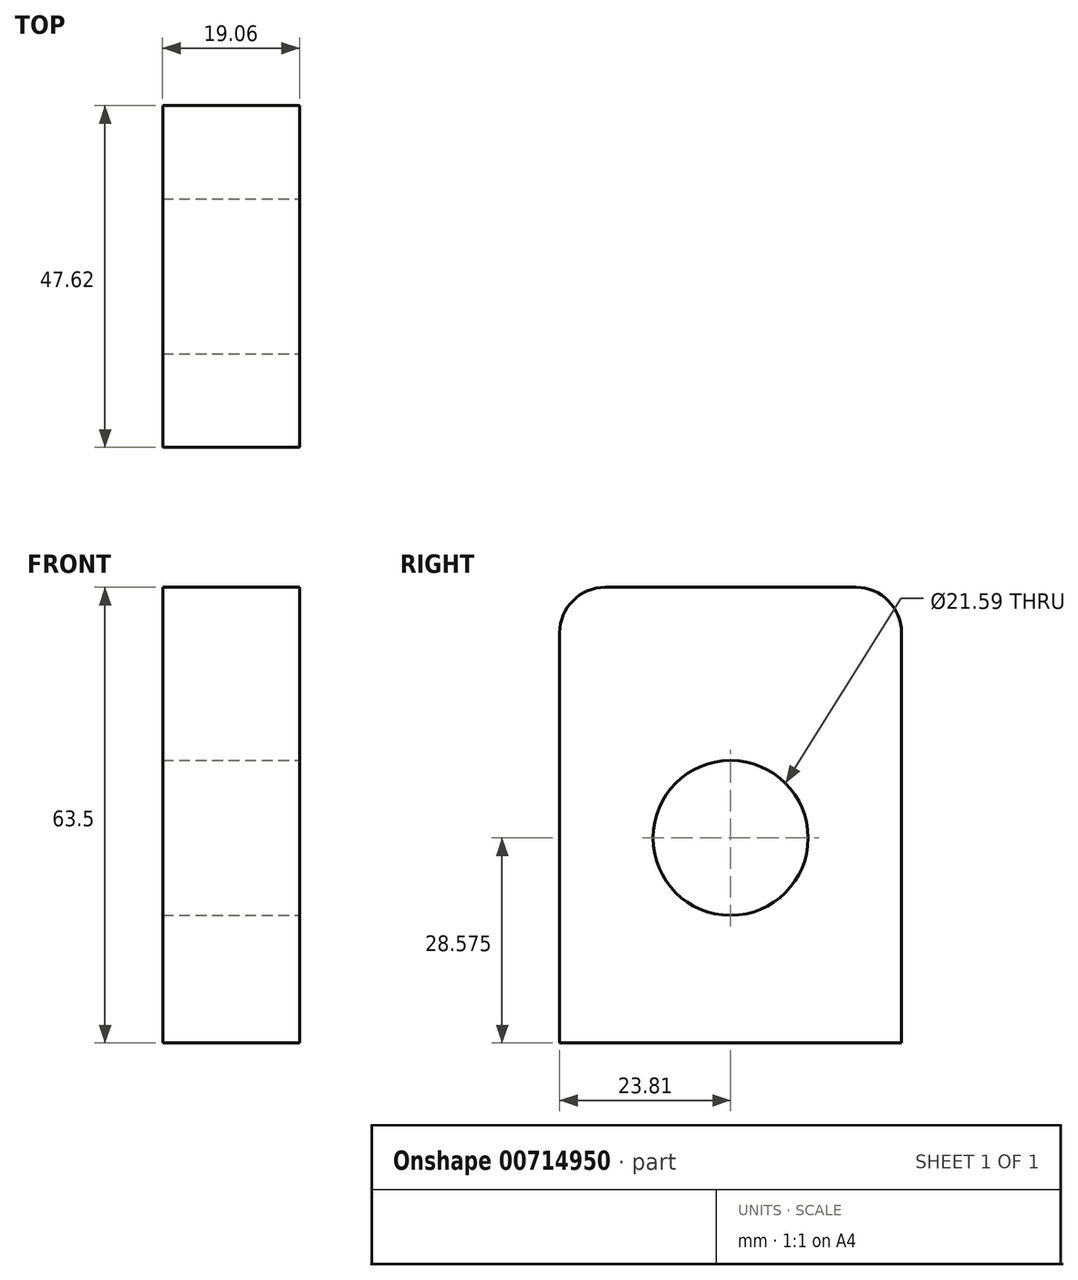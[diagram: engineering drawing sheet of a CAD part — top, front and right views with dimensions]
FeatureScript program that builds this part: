
annotation { "Feature Type Name" : "Feature", "Feature Type Description" : "" }
export const myFeature = defineFeature(function(context is Context, id is Id, definition is map)
    precondition{}
    {
        {
            var Q0;
            Q0=qCreatedBy(makeId("Right.planeOp"),FACE);
            var sketch = newSketch(context, id + "F0", { "sketchPlane" : qUnion([Q0])});
            skLineSegment(sketch, "E0.bottom", {"start": v(-23.81, -31.75) * mm, "end": v(23.81, -31.75) * mm});
            skLineSegment(sketch, "E0.top", {"start": v(-17.46, 31.75) * mm, "end": v(17.46, 31.75) * mm});
            skLineSegment(sketch, "E0.left", {"start": v(-23.81, -31.75) * mm, "end": v(-23.81, 25.4) * mm});
            skLineSegment(sketch, "E0.right", {"start": v(23.81, -31.75) * mm, "end": v(23.81, 25.4) * mm});
            skPoint(sketch, "E0.middle", {"position": v(0, 0) * mm});
            skPoint(sketch, "E1.visualSharp", {"position": v(23.81, 31.75) * mm});
            skArc(sketch, "E1.filletArc", {"start": v(23.81, 25.4) * mm, "mid": v(21.95, 29.9) * mm, "end": v(17.46, 31.75) * mm});
            skPoint(sketch, "E2.visualSharp", {"position": v(-23.81, 31.75) * mm});
            skArc(sketch, "E2.filletArc", {"start": v(-17.46, 31.75) * mm, "mid": v(-21.95, 29.9) * mm, "end": v(-23.81, 25.4) * mm});
            skSolve(sketch);
        }
        {
            var Q0;
            Q0=qSketchRegion(id+"F0",true);
            extrude(context, id + "F1", {"entities" : qUnion([Q0]), "endBound" : BoundingType.SYMMETRIC, "depth" : 19.05 * mm, "offsetDistance" : 25.4 * mm});
        }
        {
            var Q0;
            Q0=makeQuery(id+"F1.opExtrude","CAP_FACE",FACE,{"disambiguationData":[OSD([sQuery(id+"F0.wireOp",EDGE,"E0.bottom"),sQuery(id+"F0.wireOp",EDGE,"E0.top"),sQuery(id+"F0.wireOp",EDGE,"E0.left"),sQuery(id+"F0.wireOp",EDGE,"E0.right"),sQuery(id+"F0.wireOp",EDGE,"E1.filletArc"),sQuery(id+"F0.wireOp",EDGE,"E2.filletArc")])],"isStart":false});
            var sketch = newSketch(context, id + "F2", { "sketchPlane" : qUnion([Q0])});
            skCircle(sketch, "E3", {"center": v(0, -3.18) * mm, "radius": 10.8 * mm});
            skSolve(sketch);
        }
        {
            var Q0;
            Q0=qSketchRegion(id+"F2",true);
            extrude(context, id + "F3", {"entities" : qUnion([Q0]), "operationType" : NewBodyOperationType.REMOVE, "oppositeDirection" : true, "depth" : 25.4 * mm, "offsetDistance" : 25.4 * mm});
        }
    });
